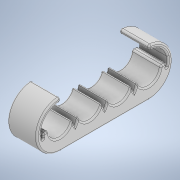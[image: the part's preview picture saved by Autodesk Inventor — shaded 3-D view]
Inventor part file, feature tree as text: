
AUTODESK INVENTOR PART (.ipt)
format: ipt  version: 2020 (Build 240168000, 168)  size: 422,400 bytes
history: native  units: in
note: dims shown in document units (in); Inventor stores cm internally (conversion verified against a paired STEP export)
features: fillet x7, extrude x1, sketch x1
ambient origin geometry x8: Origin, YZ Plane, XZ Plane, XY Plane, X Axis, Y Axis, Z Axis, Center Point
bodies: Solid1 (feature_tree)
feature tree (9):
  extrude  "Extrusion1"  Depth=0.0197in
  fillet  "Fillet1"  Radius=0.0591in
  fillet  "Fillet2"  Radius=0.0197in
  fillet  "Fillet3"  Radius=0.0591in
  fillet  "Fillet4"  Radius=0.3937in
  fillet  "Fillet5"  Radius=0.0236in
  fillet  "Fillet6"  Radius=0.1969in
  fillet  "Fillet7"  Radius=0.0236in
  sketch  "Sketch1"  dims[d2=1.5748in d4=0.3937in d5=0.3937in d7=1.0in d9=0.0197in d10=0.0591in d11=0.0197in d12=0.0591in d13=0.3937in d14=0.0in d15=0.0236in d16=0.1969in d17=0.0236in d18=0.0079in d19=0.0059in d20=0.0197in d21=0.0197in]
